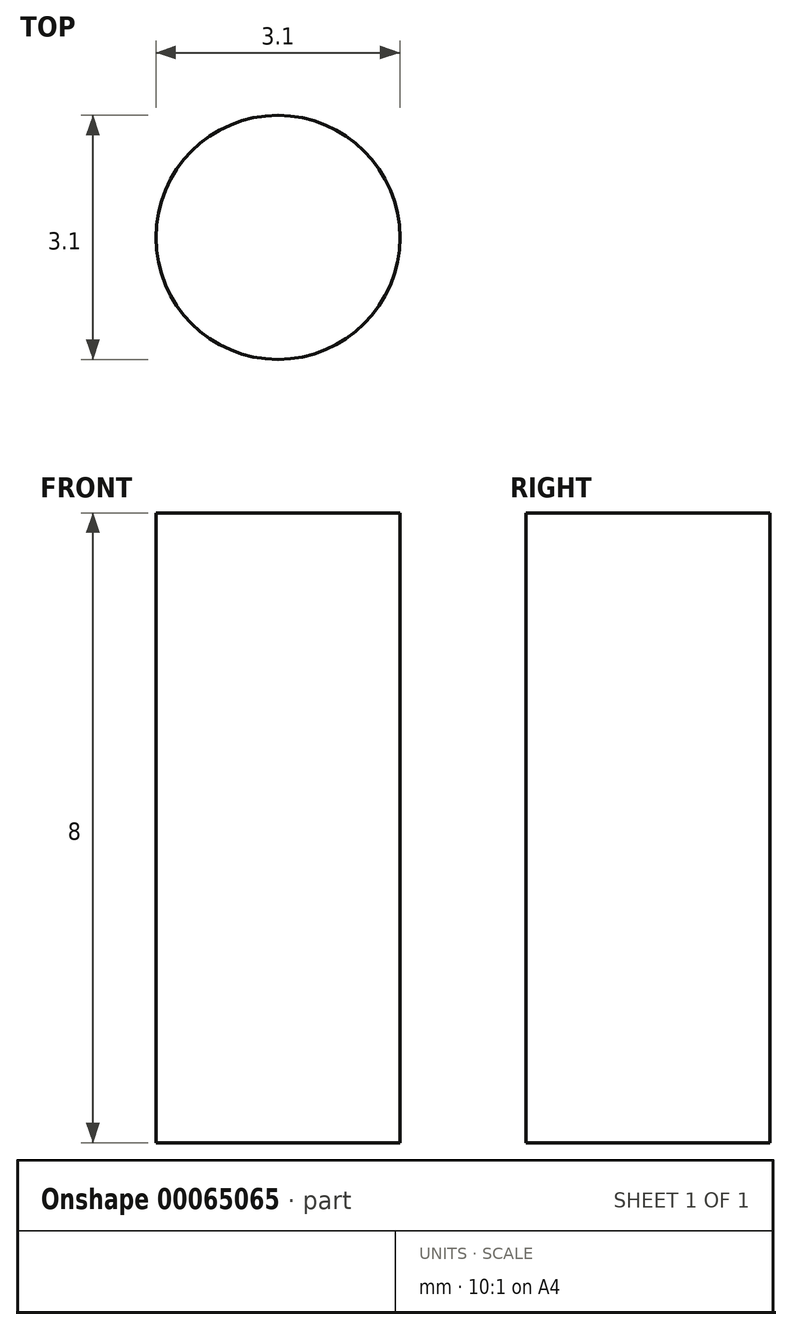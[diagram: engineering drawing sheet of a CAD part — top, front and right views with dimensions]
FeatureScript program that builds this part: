
annotation { "Feature Type Name" : "Feature", "Feature Type Description" : "" }
export const myFeature = defineFeature(function(context is Context, id is Id, definition is map)
    precondition{}
    {
        {
            var Q0;
            Q0=qCreatedBy(makeId("Front.planeOp"),FACE);
            var sketch = newSketch(context, id + "F0", { "sketchPlane" : qUnion([Q0])});
            skCircle(sketch, "E0", {"center": v(0, 0) * mm, "radius": 8 * mm});
            skLineSegment(sketch, "E1.bottom", {"start": v(-17, -9) * mm, "end": v(17, -9) * mm});
            skLineSegment(sketch, "E1.top", {"start": v(-17, -1) * mm, "end": v(-9.95, -1) * mm});
            skLineSegment(sketch, "E1.left", {"start": v(-17, -9) * mm, "end": v(-17, -1) * mm});
            skLineSegment(sketch, "E1.right", {"start": v(17, -9) * mm, "end": v(17, -1) * mm});
            skArc(sketch, "E2", {"start": v(9.95, -1) * mm, "mid": v(0, 10) * mm, "end": v(-9.95, -1) * mm});
            skLineSegment(sketch, "E3.trimOffspring", {"start": v(9.95, -1) * mm, "end": v(17, -1) * mm});
            skSolve(sketch);
        }
        {
            var Q0;
            Q0=makeQuery(id+"F0.imprint","IMPRINT",FACE,{"disambiguationData":[TD([[makeQuery(id+"F0.imprint","IMPRINT",EDGE,{"derivedFrom":sQuery(id+"F0.wireOp",EDGE,"E0")}),-1.0]])]});
            extrude(context, id + "F1", {"entities" : qUnion([Q0]), "depth" : 10 * mm, "offsetDistance" : 25.4 * mm});
        }
        {
            var Q0;
            Q0=makeQuery(id+"F1.opExtrude","SWEPT_FACE",FACE,{"disambiguationData":[OSD([sQuery(id+"F0.wireOp",EDGE,"E1.bottom")])]});
            var sketch = newSketch(context, id + "F2", { "sketchPlane" : qUnion([Q0])});
            skLineSegment(sketch, "E4", {"start": v(-17, 5) * mm, "end": v(17, 5) * mm, "construction": true});
            skCircle(sketch, "E5", {"center": v(-12, 5) * mm, "radius": 1.55 * mm});
            skCircle(sketch, "E6.MirrorC", {"center": v(12, 5) * mm, "radius": 1.55 * mm});
            skSolve(sketch);
        }
        {
            var Q0;
            Q0=makeQuery(id+"F2.imprint","IMPRINT",FACE,{"disambiguationData":[TD([[makeQuery(id+"F2.imprint","IMPRINT",EDGE,{"derivedFrom":sQuery(id+"F2.wireOp",EDGE,"E5")}),1.0]])]});
            var Q1;
            Q1=makeQuery(id+"F2.imprint","IMPRINT",FACE,{"disambiguationData":[TD([[makeQuery(id+"F2.imprint","IMPRINT",EDGE,{"derivedFrom":sQuery(id+"F2.wireOp",EDGE,"E6.MirrorC")}),-1.0]])]});
            extrude(context, id + "F3", {"entities" : qUnion([Q0, Q1]), "operationType" : NewBodyOperationType.REMOVE, "endBound" : BoundingType.UP_TO_NEXT, "oppositeDirection" : true, "depth" : 25.4 * mm, "offsetDistance" : 25.4 * mm});
        }
    });
